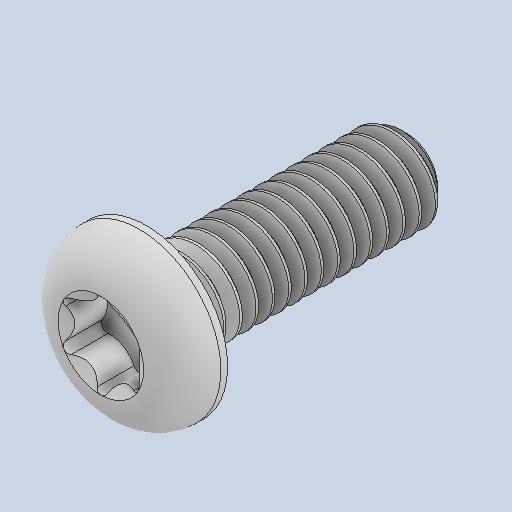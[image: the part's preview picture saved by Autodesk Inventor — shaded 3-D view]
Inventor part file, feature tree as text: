
AUTODESK INVENTOR PART (.ipt)
format: ipt  version: 2024.2 (Build 282272000, 272)  size: 658,944 bytes
history: native  units: in
note: dims shown in document units (in); Inventor stores cm internally (conversion verified against a paired STEP export)
features: extrude x1
ambient origin geometry x8: Origin, YZ Plane, XZ Plane, XY Plane, X Axis, Y Axis, Z Axis, Center Point
bodies: Solid1 (feature_tree)
feature tree (1):
  extrude  "Extrude16"  [1 undecoded]
note: 1 required parameter value undecoded (feature->parameter linkage not recoverable at this tier; creation-order binding heuristic only, values carry confidence <= 0.55)
